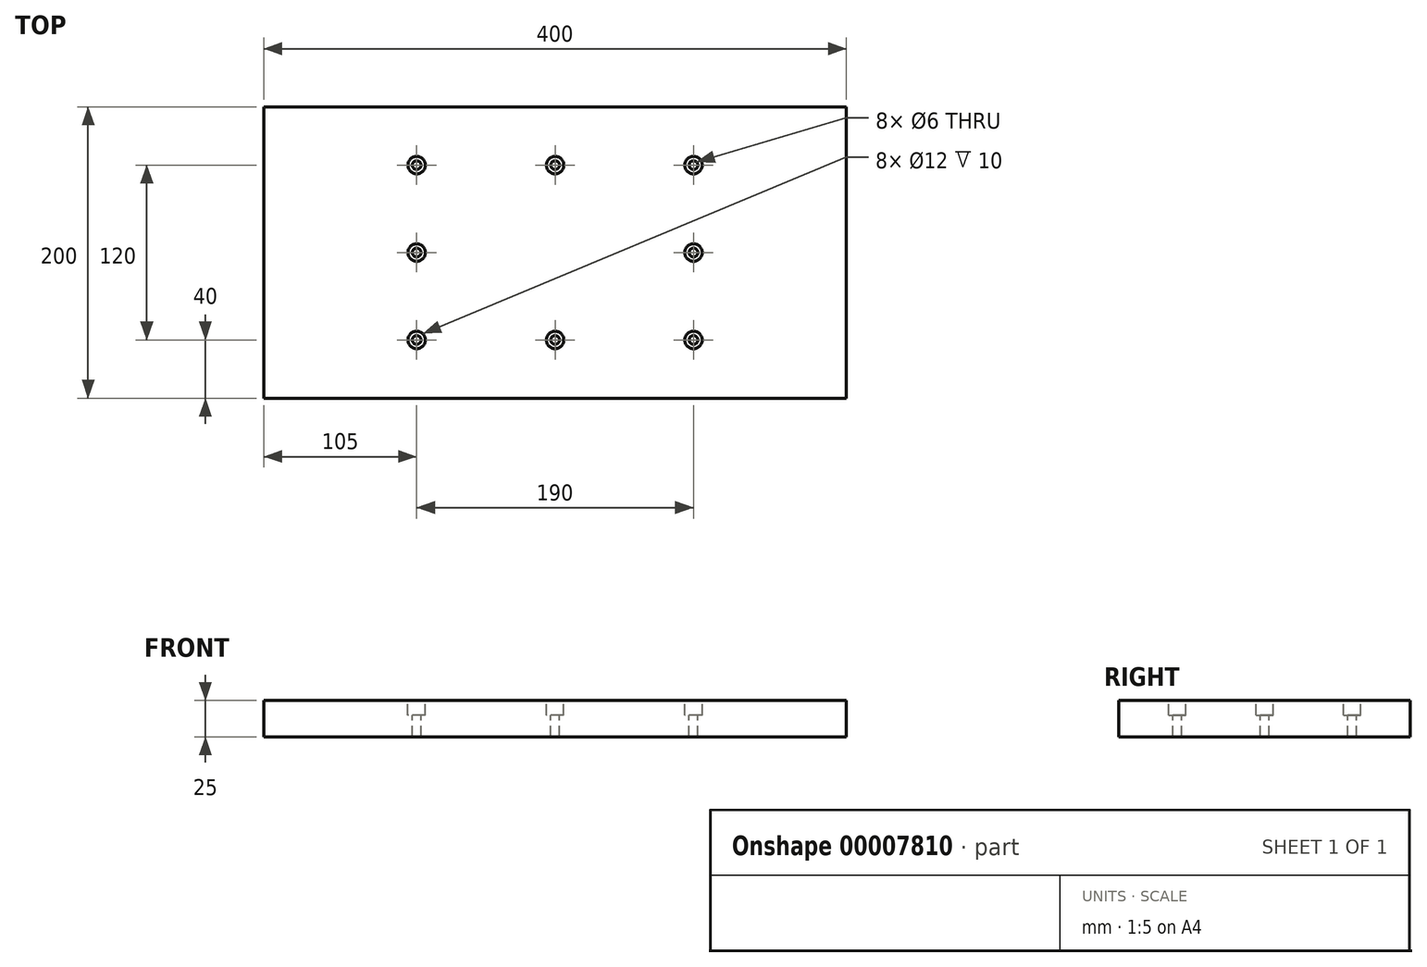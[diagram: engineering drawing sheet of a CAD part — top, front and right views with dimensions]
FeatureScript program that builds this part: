
annotation { "Feature Type Name" : "Feature", "Feature Type Description" : "" }
export const myFeature = defineFeature(function(context is Context, id is Id, definition is map)
    precondition{}
    {
        {
            var Q0;
            Q0=qCreatedBy(makeId("Top.planeOp"),FACE);
            var sketch = newSketch(context, id + "F0", { "sketchPlane" : qUnion([Q0])});
            skLineSegment(sketch, "E0.rect.bottom", {"start": v(200, 100) * mm, "end": v(-200, 100) * mm});
            skLineSegment(sketch, "E0.rect.top", {"start": v(200, -100) * mm, "end": v(-200, -100) * mm});
            skLineSegment(sketch, "E0.rect.left", {"start": v(200, 100) * mm, "end": v(200, -100) * mm});
            skLineSegment(sketch, "E0.rect.right", {"start": v(-200, 100) * mm, "end": v(-200, -100) * mm});
            skPoint(sketch, "E0.rect.middle", {"position": v(0, 0) * mm});
            skSolve(sketch);
        }
        {
            var Q0;
            Q0 = qSketchRegion(id + "F0", true);
            extrude(context, id + "F1", {"entities" : qUnion([Q0]), "depth" : 25 * mm});
        }
        {
            var Q0;
            Q0=makeQuery(id+"F1.opExtrude","CAP_FACE",FACE,{"disambiguationData":[OSD([sQuery(id+"F0.wireOp",EDGE,"E0.rect.bottom"),sQuery(id+"F0.wireOp",EDGE,"E0.rect.top"),sQuery(id+"F0.wireOp",EDGE,"E0.rect.left"),sQuery(id+"F0.wireOp",EDGE,"E0.rect.right")])],"isStart":false});
            var sketch = newSketch(context, id + "F2", { "sketchPlane" : qUnion([Q0])});
            skLineSegment(sketch, "E1.rect.bottom", {"start": v(95, 60) * mm, "end": v(-95, 60) * mm, "construction": true});
            skLineSegment(sketch, "E1.rect.top", {"start": v(95, -60) * mm, "end": v(-95, -60) * mm, "construction": true});
            skLineSegment(sketch, "E1.rect.left", {"start": v(95, 60) * mm, "end": v(95, -60) * mm, "construction": true});
            skLineSegment(sketch, "E1.rect.right", {"start": v(-95, 60) * mm, "end": v(-95, -60) * mm, "construction": true});
            skPoint(sketch, "E1.rect.middle", {"position": v(0, 0) * mm});
            skCircle(sketch, "E2", {"center": v(-95, 60) * mm, "radius": 3 * mm});
            skCircle(sketch, "E3", {"center": v(0, 60) * mm, "radius": 3 * mm});
            skCircle(sketch, "E4", {"center": v(95, 60) * mm, "radius": 3 * mm});
            skCircle(sketch, "E5", {"center": v(-95, -60) * mm, "radius": 3 * mm});
            skCircle(sketch, "E6", {"center": v(-95, 0) * mm, "radius": 3 * mm});
            skCircle(sketch, "E7", {"center": v(95, 0) * mm, "radius": 3 * mm});
            skCircle(sketch, "E8", {"center": v(95, -60) * mm, "radius": 3 * mm});
            skCircle(sketch, "E9", {"center": v(0, -60) * mm, "radius": 3 * mm});
            skCircle(sketch, "E10", {"center": v(-95, 60) * mm, "radius": 6 * mm});
            skCircle(sketch, "E11", {"center": v(0, 60) * mm, "radius": 6 * mm});
            skCircle(sketch, "E12", {"center": v(95, 60) * mm, "radius": 6 * mm});
            skCircle(sketch, "E13", {"center": v(-95, 0) * mm, "radius": 6 * mm});
            skCircle(sketch, "E14", {"center": v(95, 0) * mm, "radius": 6 * mm});
            skCircle(sketch, "E15", {"center": v(95, -60) * mm, "radius": 6 * mm});
            skCircle(sketch, "E16", {"center": v(0, -60) * mm, "radius": 6 * mm});
            skCircle(sketch, "E17", {"center": v(-95, -60) * mm, "radius": 6 * mm});
            skLineSegment(sketch, "E18.0", {"start": v(95, 75) * mm, "end": v(-95, 75) * mm});
            skLineSegment(sketch, "E19.0", {"start": v(95, -45) * mm, "end": v(-95, -45) * mm});
            skSolve(sketch);
        }
        {
            var Q0;
            Q0=makeQuery(id+"F2.imprint","IMPRINT",FACE,{"disambiguationData":[TD([[makeQuery(id+"F2.imprint","IMPRINT",EDGE,{"derivedFrom":sQuery(id+"F2.wireOp",EDGE,"E2")}),1.0]])]});
            var Q1;
            Q1=makeQuery(id+"F2.imprint","IMPRINT",FACE,{"disambiguationData":[TD([[makeQuery(id+"F2.imprint","IMPRINT",EDGE,{"derivedFrom":sQuery(id+"F2.wireOp",EDGE,"E3")}),1.0]])]});
            var Q2;
            Q2=makeQuery(id+"F2.imprint","IMPRINT",FACE,{"disambiguationData":[TD([[makeQuery(id+"F2.imprint","IMPRINT",EDGE,{"derivedFrom":sQuery(id+"F2.wireOp",EDGE,"E6")}),1.0]])]});
            var Q3;
            Q3=makeQuery(id+"F2.imprint","IMPRINT",FACE,{"disambiguationData":[TD([[makeQuery(id+"F2.imprint","IMPRINT",EDGE,{"derivedFrom":sQuery(id+"F2.wireOp",EDGE,"E5")}),1.0]])]});
            var Q4;
            Q4=makeQuery(id+"F2.imprint","IMPRINT",FACE,{"disambiguationData":[TD([[makeQuery(id+"F2.imprint","IMPRINT",EDGE,{"derivedFrom":sQuery(id+"F2.wireOp",EDGE,"E9")}),1.0]])]});
            var Q5;
            Q5=makeQuery(id+"F2.imprint","IMPRINT",FACE,{"disambiguationData":[TD([[makeQuery(id+"F2.imprint","IMPRINT",EDGE,{"derivedFrom":sQuery(id+"F2.wireOp",EDGE,"E7")}),1.0]])]});
            var Q6;
            Q6=makeQuery(id+"F2.imprint","IMPRINT",FACE,{"disambiguationData":[TD([[makeQuery(id+"F2.imprint","IMPRINT",EDGE,{"derivedFrom":sQuery(id+"F2.wireOp",EDGE,"E8")}),1.0]])]});
            var Q7;
            Q7=makeQuery(id+"F2.imprint","IMPRINT",FACE,{"disambiguationData":[TD([[makeQuery(id+"F2.imprint","IMPRINT",EDGE,{"derivedFrom":sQuery(id+"F2.wireOp",EDGE,"E4")}),1.0]])]});
            extrude(context, id + "F3", {"entities" : qUnion([Q0, Q1, Q2, Q3, Q4, Q5, Q6, Q7]), "operationType" : NewBodyOperationType.REMOVE, "endBound" : BoundingType.THROUGH_ALL, "oppositeDirection" : true, "depth" : 25 * mm});
        }
        {
            var Q0;
            Q0=makeQuery(id+"F2.imprint","IMPRINT",FACE,{"disambiguationData":[TD([[makeQuery(id+"F2.imprint","IMPRINT",EDGE,{"derivedFrom":sQuery(id+"F2.wireOp",EDGE,"E2")}),-1.0]])]});
            var Q1;
            Q1=makeQuery(id+"F2.imprint","IMPRINT",FACE,{"disambiguationData":[TD([[makeQuery(id+"F2.imprint","IMPRINT",EDGE,{"derivedFrom":sQuery(id+"F2.wireOp",EDGE,"E3")}),-1.0]])]});
            var Q2;
            Q2=makeQuery(id+"F2.imprint","IMPRINT",FACE,{"disambiguationData":[TD([[makeQuery(id+"F2.imprint","IMPRINT",EDGE,{"derivedFrom":sQuery(id+"F2.wireOp",EDGE,"E4")}),-1.0]])]});
            var Q3;
            Q3=makeQuery(id+"F2.imprint","IMPRINT",FACE,{"disambiguationData":[TD([[makeQuery(id+"F2.imprint","IMPRINT",EDGE,{"derivedFrom":sQuery(id+"F2.wireOp",EDGE,"E7")}),-1.0]])]});
            var Q4;
            Q4=makeQuery(id+"F2.imprint","IMPRINT",FACE,{"disambiguationData":[TD([[makeQuery(id+"F2.imprint","IMPRINT",EDGE,{"derivedFrom":sQuery(id+"F2.wireOp",EDGE,"E6")}),-1.0]])]});
            var Q5;
            Q5=makeQuery(id+"F2.imprint","IMPRINT",FACE,{"disambiguationData":[TD([[makeQuery(id+"F2.imprint","IMPRINT",EDGE,{"derivedFrom":sQuery(id+"F2.wireOp",EDGE,"E5")}),-1.0]])]});
            var Q6;
            Q6=makeQuery(id+"F2.imprint","IMPRINT",FACE,{"disambiguationData":[TD([[makeQuery(id+"F2.imprint","IMPRINT",EDGE,{"derivedFrom":sQuery(id+"F2.wireOp",EDGE,"E9")}),-1.0]])]});
            var Q7;
            Q7=makeQuery(id+"F2.imprint","IMPRINT",FACE,{"disambiguationData":[TD([[makeQuery(id+"F2.imprint","IMPRINT",EDGE,{"derivedFrom":sQuery(id+"F2.wireOp",EDGE,"E8")}),-1.0]])]});
            extrude(context, id + "F4", {"entities" : qUnion([Q0, Q1, Q2, Q3, Q4, Q5, Q6, Q7]), "operationType" : NewBodyOperationType.REMOVE, "oppositeDirection" : true, "depth" : 10 * mm});
        }
    });
